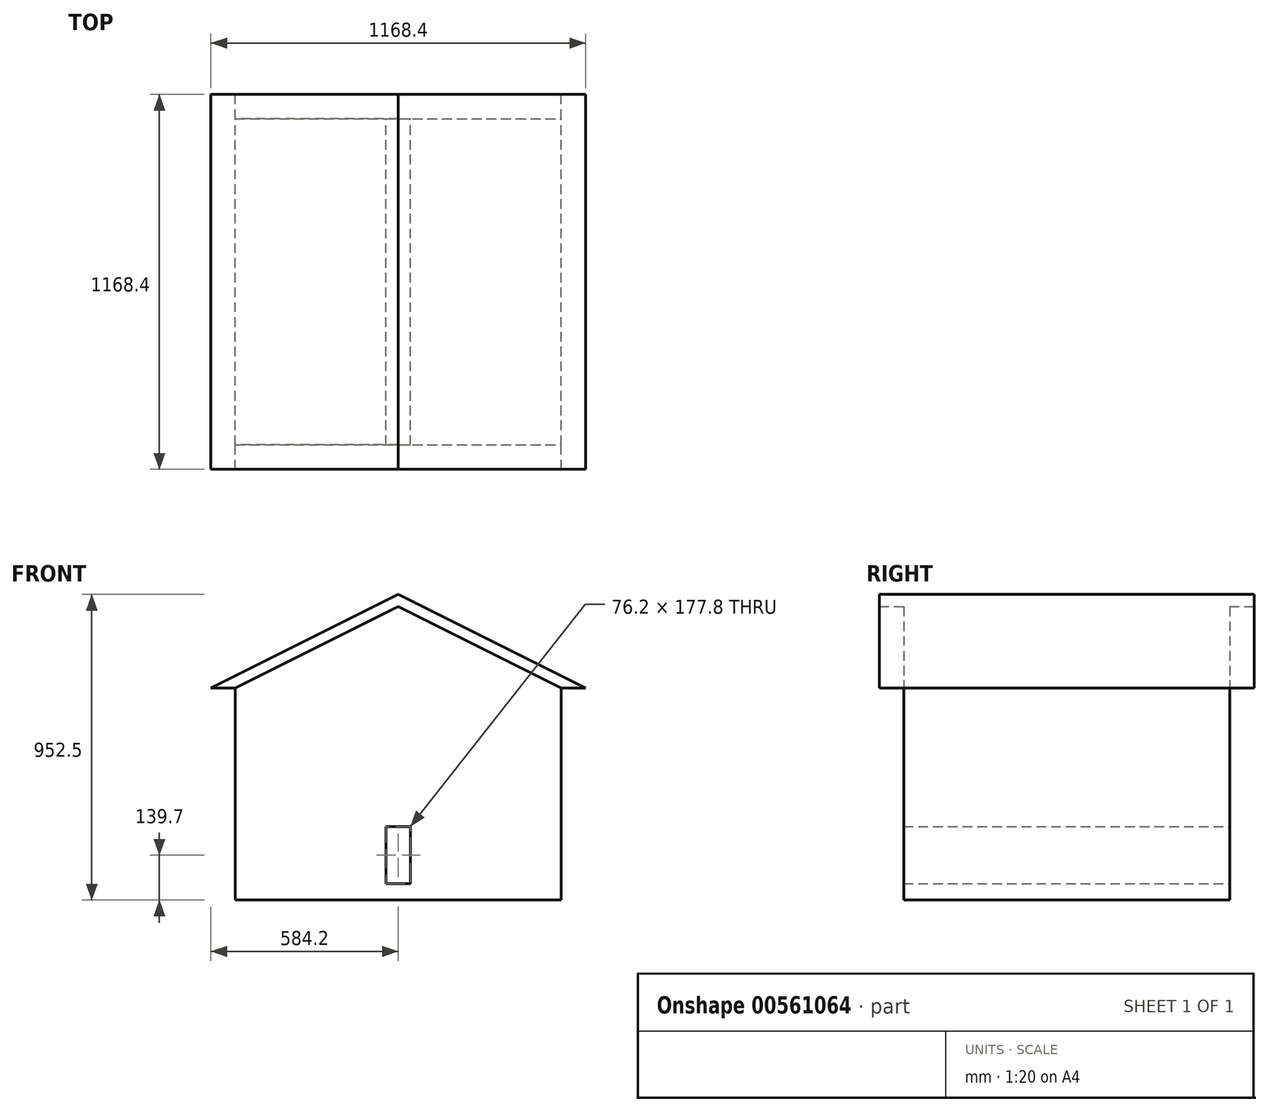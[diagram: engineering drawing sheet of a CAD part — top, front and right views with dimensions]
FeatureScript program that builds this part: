
annotation { "Feature Type Name" : "Feature", "Feature Type Description" : "" }
export const myFeature = defineFeature(function(context is Context, id is Id, definition is map)
    precondition{}
    {
        {
            var Q0;
            Q0=qCreatedBy(makeId("Front.planeOp"),FACE);
            var sketch = newSketch(context, id + "F0", { "sketchPlane" : qUnion([Q0])});
            skLineSegment(sketch, "E0", {"start": v(0, 0) * mm, "end": v(-508, 0) * mm});
            skLineSegment(sketch, "E1", {"start": v(0, 0) * mm, "end": v(508, 0) * mm});
            skLineSegment(sketch, "E2", {"start": v(0, 0) * mm, "end": v(0, 254) * mm});
            skLineSegment(sketch, "E3", {"start": v(0, 254) * mm, "end": v(-508, 0) * mm});
            skLineSegment(sketch, "E4", {"start": v(0, 254) * mm, "end": v(508, 0) * mm});
            skLineSegment(sketch, "E5", {"start": v(0, 254) * mm, "end": v(0, 292.1) * mm});
            skLineSegment(sketch, "E6", {"start": v(-508, 0) * mm, "end": v(-584.2, 0) * mm});
            skLineSegment(sketch, "E7", {"start": v(508, 0) * mm, "end": v(584.2, 0) * mm});
            skLineSegment(sketch, "E8", {"start": v(0, 292.1) * mm, "end": v(-584.2, 0) * mm});
            skLineSegment(sketch, "E9", {"start": v(0, 292.1) * mm, "end": v(584.2, 0) * mm});
            skLineSegment(sketch, "E10", {"start": v(-508, 0) * mm, "end": v(-508, -609.6) * mm});
            skLineSegment(sketch, "E11", {"start": v(508, 0) * mm, "end": v(508, -609.6) * mm});
            skLineSegment(sketch, "E12", {"start": v(-508, -609.6) * mm, "end": v(508, -609.6) * mm});
            skLineSegment(sketch, "E13", {"start": v(0, -609.6) * mm, "end": v(-38.1, -609.6) * mm});
            skLineSegment(sketch, "E14", {"start": v(-38.1, -609.6) * mm, "end": v(-38.1, -431.8) * mm});
            skLineSegment(sketch, "E15", {"start": v(-38.1, -431.8) * mm, "end": v(38.1, -431.8) * mm});
            skLineSegment(sketch, "E16", {"start": v(0, -609.6) * mm, "end": v(38.1, -609.6) * mm});
            skLineSegment(sketch, "E17", {"start": v(38.1, -431.8) * mm, "end": v(38.1, -609.6) * mm});
            skLineSegment(sketch, "E18", {"start": v(-508, -609.6) * mm, "end": v(-508, -660.4) * mm});
            skLineSegment(sketch, "E19", {"start": v(508, -609.6) * mm, "end": v(508, -660.4) * mm});
            skLineSegment(sketch, "E20", {"start": v(-508, -660.4) * mm, "end": v(508, -660.4) * mm});
            skLineSegment(sketch, "E21", {"start": v(-38.1, -609.6) * mm, "end": v(38.1, -609.6) * mm});
            skLineSegment(sketch, "E22", {"start": v(-38.1, -609.6) * mm, "end": v(-38.1, -660.4) * mm});
            skLineSegment(sketch, "E23", {"start": v(-38.1, -660.4) * mm, "end": v(38.1, -660.4) * mm});
            skLineSegment(sketch, "E24", {"start": v(38.1, -660.4) * mm, "end": v(38.1, -609.6) * mm});
            skSolve(sketch);
        }
        {
            var Q0;
            Q0=makeQuery(id+"F0.imprint","IMPRINT",FACE,{"disambiguationData":[TD([[makeQuery(id+"F0.imprint","IMPRINT",EDGE,{"derivedFrom":sQuery(id+"F0.wireOp",EDGE,"E3")}),-1.0]])]});
            var Q1;
            Q1=makeQuery(id+"F0.imprint","IMPRINT",FACE,{"disambiguationData":[TD([[makeQuery(id+"F0.imprint","IMPRINT",EDGE,{"derivedFrom":sQuery(id+"F0.wireOp",EDGE,"E4")}),1.0]])]});
            extrude(context, id + "F1", {"entities" : qUnion([Q0, Q1]), "endBound" : BoundingType.SYMMETRIC, "depth" : 1168.4 * mm, "offsetDistance" : 25.4 * mm});
        }
        {
            var Q0;
            Q0 = qSketchRegion(id + "F0", true);
            extrude(context, id + "F2", {"entities" : qUnion([Q0]), "operationType" : NewBodyOperationType.ADD, "endBound" : BoundingType.SYMMETRIC, "depth" : 1016 * mm, "offsetDistance" : 25.4 * mm});
        }
    });
